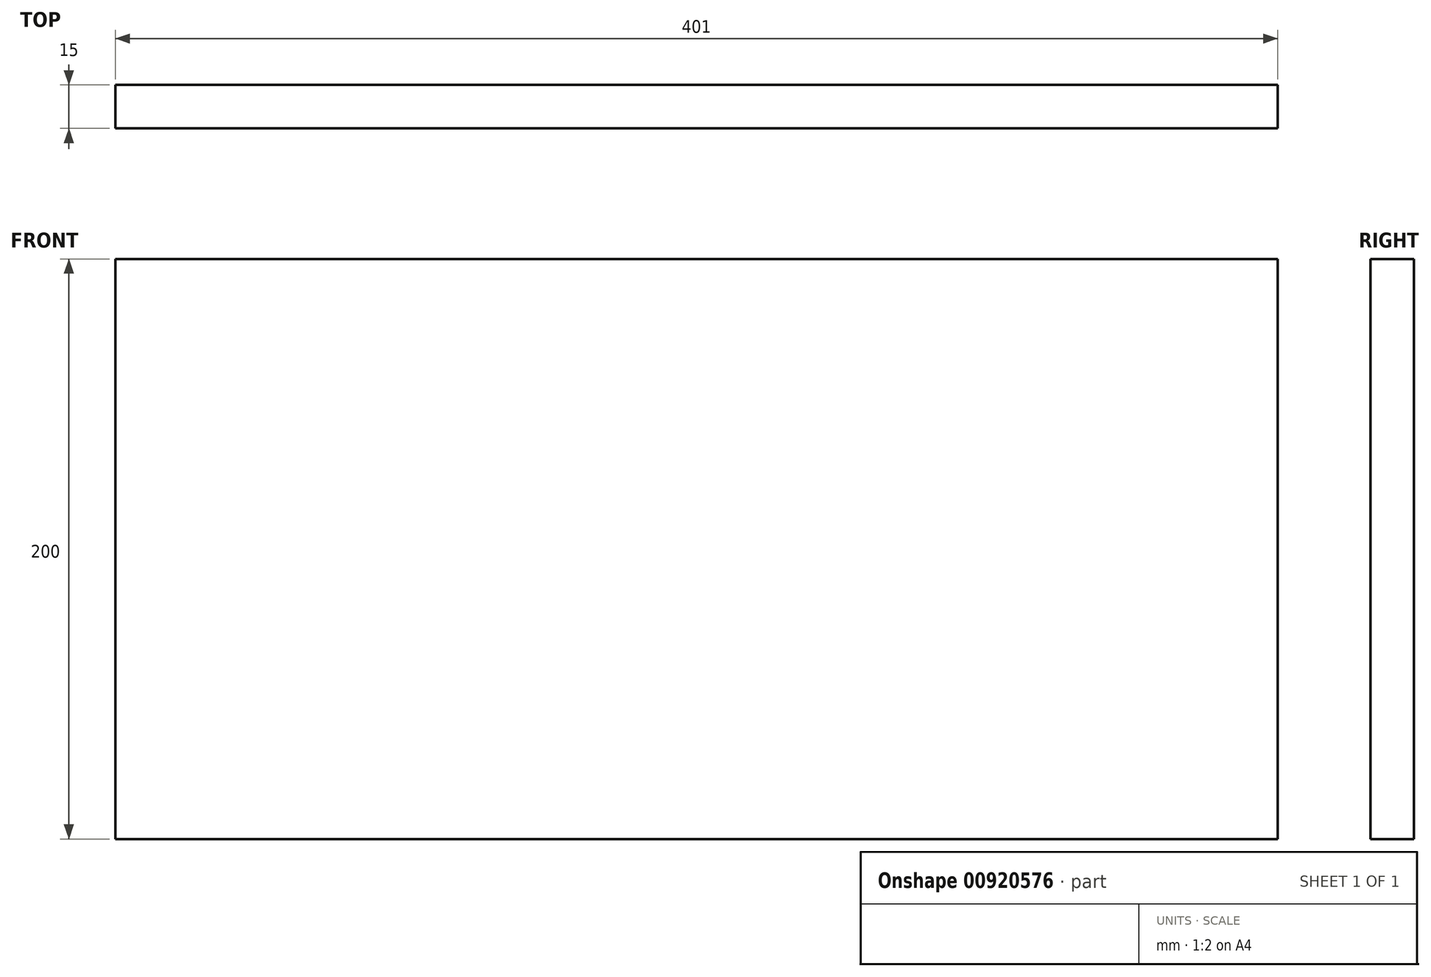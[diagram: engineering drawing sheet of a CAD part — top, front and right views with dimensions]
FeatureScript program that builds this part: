
annotation { "Feature Type Name" : "Feature", "Feature Type Description" : "" }
export const myFeature = defineFeature(function(context is Context, id is Id, definition is map)
    precondition{}
    {
        {
            var Q0;
            Q0=qCreatedBy(makeId("Front.planeOp"),FACE);
            var sketch = newSketch(context, id + "F0", { "sketchPlane" : qUnion([Q0])});
            skLineSegment(sketch, "E0.bottom", {"start": v(200.5, 100) * mm, "end": v(-200.5, 100) * mm});
            skLineSegment(sketch, "E0.top", {"start": v(200.5, -100) * mm, "end": v(-200.5, -100) * mm});
            skLineSegment(sketch, "E0.left", {"start": v(200.5, 100) * mm, "end": v(200.5, -100) * mm});
            skLineSegment(sketch, "E0.right", {"start": v(-200.5, 100) * mm, "end": v(-200.5, -100) * mm});
            skPoint(sketch, "E0.middle", {"position": v(0, 0) * mm});
            skSolve(sketch);
        }
        {
            var Q0;
            Q0=qSketchRegion(id+"F0",true);
            extrude(context, id + "F1", {"entities" : qUnion([Q0]), "depth" : 15 * mm, "symmetric" : true});
        }
    });
